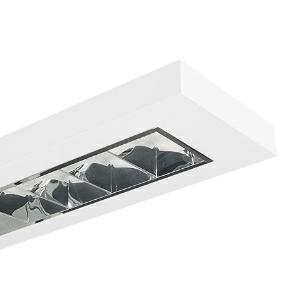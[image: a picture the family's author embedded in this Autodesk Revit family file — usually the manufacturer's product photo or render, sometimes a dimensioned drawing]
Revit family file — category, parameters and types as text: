
# Revit family: 3f_filippi_-_3f_travetta_tunable_white_2mg_3f_filippi_-_10763_-_3f_trav__led_2x22w_dali_dt8_tw_2mg_l1590__cct_2700__b9a6
name_source: partatom
category: Lighting Fixtures
units: mm (PartAtom-declared; Revit-internal decimal feet)

## family parameters
Cut with Voids When Loaded = No
Host = Face
Light Source = No
Part Type = Normal
Room Calculation Point = No
Round Connector Dimension = Use Diameter
Shared = No

## types (1)
- 3F Filippi - 3F Travetta Tunable White 2MG (1 x LED, 5800 lm, 50 W, 2700 K)
    Apparent Load = 50 VA
    Approval mark = ENEC
    CIE Flux Codes = 72 99 100 100 100
    Color Rendering = 80
    Color Temperature = 2700 K
    Control Gear = Electronic transformer
    Default Elevation = 1800 mm
    Description = ILLUMINOTECHNICAL
Luminous efficiency 100% (DLOR 100%, ULOR 0%).
Luminaire luminous flux 5800 lm @ 2700 K.
Luminaire luminous flux 6236 lm @ 4000 K.
Luminaire luminous flux 6236 lm @ 6500 K.
Direct symmetric distribution.
Installation Interdistance Transv.D = 1.29 x hu - Long.D = 1.23 x hu.
Average luminance <1000 cd/m² for radial angles >65°.
Tabular UGR (CIE 117 - 4H-8H; S=0.25H; 70/50/20): RUG 16.8 - 19.
Beam angle: 80° - 84°.
Luminous efficacy 116 lm/W.
Lifetime (L90/B10): 30000 h. (tq+25°C)
Lifetime (L85/B10): 50000 h. (tq+25°C)
Lifetime (L75/B10): 80000 h. (tq+25°C)
Lifetime (L70/B10): 100000 h. (tq+25°C)
Sudden decreased luminous flux after 50000 hours: 0% (C0).
Photobiological safety in compliance with IEC/TR 62778: RG0 risk exempt, (IEC 62471).
In compliance with IEC/EN 62722-2-1 - IEC/EN 62717 standards.

SOURCE
2 linear LED modules 22W/TW.
Energy efficiency class (UE 2019/2020 - UE 2019/2015): D.
CIE 13.3 Colour rendering index: CRI >80 (R9 <50%).
IES TM-30 Fidelity Index: Rf = 84 Rg = 95.
The colour temperature can be adjusted between 2700 K and 6500 K.
Colour initial tolerance (MacAdam): SDCM 2.

MECHANICAL
Housing with squared shape in white painted galvannealed steel, with nonreflecting surface.
2MG parabolic louvre, high efficiency, in specular aluminium with superficial titanium-magnesium treatment, non-iridescent, with transverse blades closed at the top.
Prismatic flat diffuser in transparent methacrylate (PMMA), multilenticular, anti-glare, prismatic exterior, placed above louvre blades.
Film protective against dust and finger marks, adhesive, attached to louvre.
Luminaire with limited surface temperature. - D - (EN 60598-2-24)
Dimensions: 1590x190 mm, height 60 mm (edge 40 mm). Weight 5.35 kg.
IP20 protection degree.
Mechanical strength to impacts IK02 (0.2 joule).
Glow-wire test resistance 650°C.

ELECTRICAL
Halogen Free DALI DT8, PUSH-DIM, electronic wiring 230V-50/60Hz, power factor 0.95, THD <25%, constant output power, SELV, class I, 1 driver, 1 DALI addresse.
Power of the luminaire 50 W.
CE - IEC 60598-1 - EN 60598-1.
SAFE FLICKER: PstLM=<1 and SVM=<0.4 (IEC TR 61547-1 and IEC TR 63158), to ensure a more comfortable and safe light.
Luminaire compliant with EN 60598-2-22 for power supply from a centralised emergency system CPSS (Central Power Supply System), not incorporated in the luminaire - high risk areas excluded. The default power and flux are 100% in AC and 15% in DC.
Ambient temperature from 0°C to +25°C.
Temperature class T6 max 85°C.
5-pole terminal block (L-N-PE-DA/DA) for line connection with connection capacity 2x2.5 mm².
Relative humidity UR: <85%.

INSTALLATION
Suspended.
All accessories dedicated to this product are available on the Catalog and on our website www.3F-Filippi.com.

APPLICATIONS
Any environments requiring light which aims for the wellness of people.
In environments, even with reduced height, requiring a comfortable light. Offices with VDTs, managerial offices and staterooms.

LIGHT MANAGEMENT
Recommended minimum setting: 10%.
The luminaire, equipped with DALI DT8 driver, is designed for adjusting the luminous flux and colour temperature; can be controlled manually or automatically/manually with 3F HCL technology or 3F Bluetooth.

WARNING
Luminaire designed for disposal/recycling at end-of-life.
Replaceable (LED only) light source by a professional. Replaceable control gear by a professional.
    Height = 60 mm  [stored 0.19685 ft]
    Lamp = 1 x LED
    Lamp Light Flux = 5800 lm
    Lamp Power = 50 W
    Lamp count = 1
    Length = 1590 mm
    Lifetime = 50000 h
    Luminous efficacy = 116 lm/W
    Manufacturer = 3F Filippi
    ModVariant = No
    Model = 3F Filippi - 10763 - 3F TRAV. LED 2X22W DALI DT8 TW 2MG L1590 (CCT 2700)
    Mounting Place = Ceiling
    Mounting Type = Pendant
    Number of Poles = 1
    OnlyDefault = Yes
    Power Factor = 1
    Product Name = 3F Filippi - 3F Travetta Tunable White 2MG
    Product group = pendant luminaire
    ProductGroupID = 9
    Protection Class = Protection class I
    Protection Degree = IP 20
    RLX_Detail_Level = 1
    RLX_Emergency_Light_Flux = 0 lm
    RLX_Emergency_Type = 0
    RLX_Emergency_Type_DB = No
    RlxData = <blob elided: 56397 chars, md5=c9d57fd4>
    Socket = socket
    Standby Power = 0 W
    System Light Flux = 5800 lm
    System Power = 50 W
    Type Comments = Product without accessories
    Type Image = 3ffilippi_3f_travetta_led_2mg.jpg
    URL = http://relux.com
    VarID = ---
    Voltage = 0 V
    Weight = 0.00 kg
    Width = 190 mm  [stored 0.62336 ft]

note: [stored X ft] marks values corroborated as IEEE doubles in the binary element streams (Revit-internal decimal feet)

## geometry (parser evidence)
native form markers: Blend x4, Sweep x11
no freeform markers — native parametric forms only
